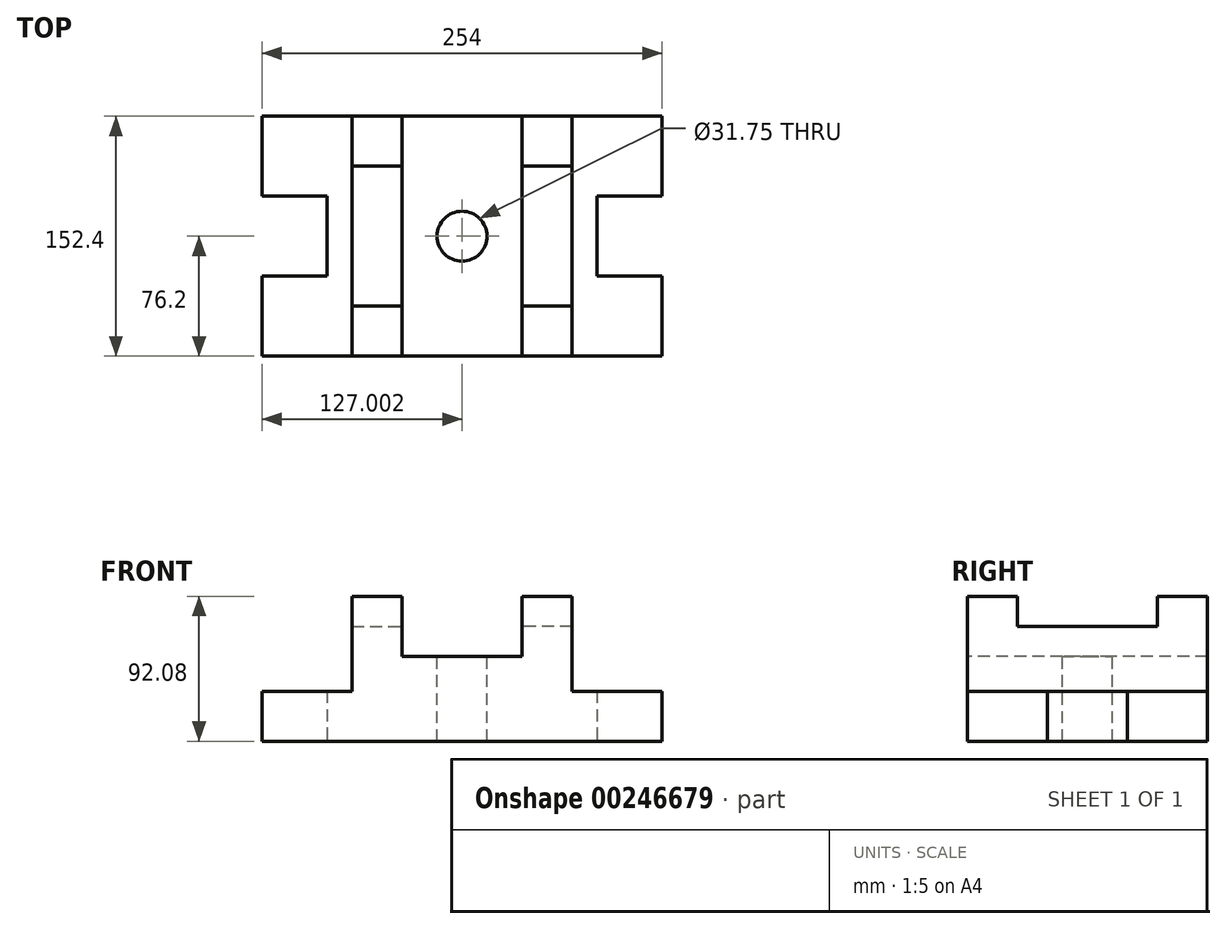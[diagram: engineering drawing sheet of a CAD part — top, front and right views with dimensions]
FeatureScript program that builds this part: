
annotation { "Feature Type Name" : "Feature", "Feature Type Description" : "" }
export const myFeature = defineFeature(function(context is Context, id is Id, definition is map)
    precondition{}
    {
        {
            var Q0;
            Q0=qCreatedBy(makeId("Top.planeOp"),FACE);
            var sketch = newSketch(context, id + "F0", { "sketchPlane" : qUnion([Q0])});
            skLineSegment(sketch, "E0.bottom", {"start": v(-124.69, 50.8) * mm, "end": v(129.31, 50.8) * mm});
            skLineSegment(sketch, "E0.top", {"start": v(-124.69, -101.6) * mm, "end": v(129.31, -101.6) * mm});
            skLineSegment(sketch, "E0.left", {"start": v(-124.69, 50.8) * mm, "end": v(-124.69, 0) * mm});
            skLineSegment(sketch, "E0.right", {"start": v(129.31, 50.8) * mm, "end": v(129.31, 0) * mm});
            skLineSegment(sketch, "E1", {"start": v(129.31, -101.6) * mm, "end": v(129.31, -50.8) * mm});
            skLineSegment(sketch, "E2", {"start": v(129.31, -50.8) * mm, "end": v(88.04, -50.8) * mm});
            skLineSegment(sketch, "E3", {"start": v(129.31, 0) * mm, "end": v(88.04, 0) * mm});
            skLineSegment(sketch, "E4", {"start": v(88.04, 0) * mm, "end": v(88.04, -50.8) * mm});
            skLineSegment(sketch, "E5.trimOffspring", {"start": v(129.31, -50.8) * mm, "end": v(129.31, -101.6) * mm});
            skLineSegment(sketch, "E6", {"start": v(-124.69, -101.6) * mm, "end": v(-124.69, -50.8) * mm});
            skLineSegment(sketch, "E7", {"start": v(-124.69, -50.8) * mm, "end": v(-83.41, -50.8) * mm});
            skLineSegment(sketch, "E8", {"start": v(-124.69, 0) * mm, "end": v(-83.41, 0) * mm});
            skLineSegment(sketch, "E9", {"start": v(-83.41, 0) * mm, "end": v(-83.41, -50.8) * mm});
            skLineSegment(sketch, "E10.trimOffspring", {"start": v(-124.69, -50.8) * mm, "end": v(-124.69, -101.6) * mm});
            skSolve(sketch);
        }
        {
            var Q0;
            Q0=makeQuery(id+"F0.imprint","IMPRINT",FACE,{"disambiguationData":[TD([[makeQuery(id+"F0.imprint","IMPRINT",EDGE,{"derivedFrom":sQuery(id+"F0.wireOp",EDGE,"E0.bottom")}),-1.0]])]});
            extrude(context, id + "F1", {"entities" : qUnion([Q0]), "depth" : 31.75 * mm});
        }
        {
            var Q0;
            Q0=makeQuery(id+"F1.opExtrude","CAP_FACE",FACE,{"disambiguationData":[OSD([sQuery(id+"F0.wireOp",EDGE,"E0.bottom"),sQuery(id+"F0.wireOp",EDGE,"E0.top"),sQuery(id+"F0.wireOp",EDGE,"E0.right"),sQuery(id+"F0.wireOp",EDGE,"E2"),sQuery(id+"F0.wireOp",EDGE,"E3"),sQuery(id+"F0.wireOp",EDGE,"E4"),sQuery(id+"F0.wireOp",EDGE,"E5.trimOffspring"),sQuery(id+"F0.wireOp",EDGE,"E0.left"),sQuery(id+"F0.wireOp",EDGE,"E7"),sQuery(id+"F0.wireOp",EDGE,"E8"),sQuery(id+"F0.wireOp",EDGE,"E9"),sQuery(id+"F0.wireOp",EDGE,"E10.trimOffspring")])],"isStart":false});
            var sketch = newSketch(context, id + "F2", { "sketchPlane" : qUnion([Q0])});
            skLineSegment(sketch, "E11", {"start": v(-124.69, -101.6) * mm, "end": v(-67.54, -101.6) * mm});
            skLineSegment(sketch, "E12.bottom", {"start": v(-67.54, -101.6) * mm, "end": v(-35.79, -101.6) * mm});
            skLineSegment(sketch, "E12.top", {"start": v(-67.54, -69.85) * mm, "end": v(-35.79, -69.85) * mm});
            skLineSegment(sketch, "E12.left", {"start": v(-67.54, -101.6) * mm, "end": v(-67.54, -69.85) * mm});
            skLineSegment(sketch, "E12.right", {"start": v(-35.79, -101.6) * mm, "end": v(-35.79, -69.85) * mm});
            skLineSegment(sketch, "E13", {"start": v(129.31, -101.6) * mm, "end": v(72.16, -101.6) * mm});
            skLineSegment(sketch, "E14.bottom", {"start": v(72.16, -101.6) * mm, "end": v(40.41, -101.6) * mm});
            skLineSegment(sketch, "E14.top", {"start": v(72.16, -69.85) * mm, "end": v(40.41, -69.85) * mm});
            skLineSegment(sketch, "E14.left", {"start": v(72.16, -101.6) * mm, "end": v(72.16, -69.85) * mm});
            skLineSegment(sketch, "E14.right", {"start": v(40.41, -101.6) * mm, "end": v(40.41, -69.85) * mm});
            skLineSegment(sketch, "E15", {"start": v(-124.69, 50.8) * mm, "end": v(-67.54, 50.8) * mm});
            skLineSegment(sketch, "E16.bottom", {"start": v(-67.54, 50.8) * mm, "end": v(-35.79, 50.8) * mm});
            skLineSegment(sketch, "E16.top", {"start": v(-67.54, 19.05) * mm, "end": v(-35.79, 19.05) * mm});
            skLineSegment(sketch, "E16.left", {"start": v(-67.54, 50.8) * mm, "end": v(-67.54, 19.05) * mm});
            skLineSegment(sketch, "E16.right", {"start": v(-35.79, 50.8) * mm, "end": v(-35.79, 19.05) * mm});
            skLineSegment(sketch, "E17", {"start": v(129.31, 50.8) * mm, "end": v(72.16, 50.8) * mm});
            skLineSegment(sketch, "E18.bottom", {"start": v(72.16, 50.8) * mm, "end": v(40.41, 50.8) * mm});
            skLineSegment(sketch, "E18.top", {"start": v(72.16, 19.05) * mm, "end": v(40.41, 19.05) * mm});
            skLineSegment(sketch, "E18.left", {"start": v(72.16, 50.8) * mm, "end": v(72.16, 19.05) * mm});
            skLineSegment(sketch, "E18.right", {"start": v(40.41, 50.8) * mm, "end": v(40.41, 19.05) * mm});
            skSolve(sketch);
        }
        {
            var Q0;
            Q0=makeQuery(id+"F2.imprint","IMPRINT",FACE,{"disambiguationData":[TD([[makeQuery(id+"F2.imprint","IMPRINT",EDGE,{"derivedFrom":sQuery(id+"F2.wireOp",EDGE,"E14.bottom")}),1.0]])]});
            var Q1;
            Q1=makeQuery(id+"F2.imprint","IMPRINT",FACE,{"disambiguationData":[TD([[makeQuery(id+"F2.imprint","IMPRINT",EDGE,{"derivedFrom":sQuery(id+"F2.wireOp",EDGE,"E18.bottom")}),-1.0]])]});
            var Q2;
            Q2=makeQuery(id+"F2.imprint","IMPRINT",FACE,{"disambiguationData":[TD([[makeQuery(id+"F2.imprint","IMPRINT",EDGE,{"derivedFrom":sQuery(id+"F2.wireOp",EDGE,"E12.bottom")}),1.0]])]});
            var Q3;
            Q3=makeQuery(id+"F2.imprint","IMPRINT",FACE,{"disambiguationData":[TD([[makeQuery(id+"F2.imprint","IMPRINT",EDGE,{"derivedFrom":sQuery(id+"F2.wireOp",EDGE,"E16.bottom")}),-1.0]])]});
            extrude(context, id + "F3", {"entities" : qUnion([Q0, Q1, Q2, Q3]), "operationType" : NewBodyOperationType.ADD, "depth" : 60.32 * mm});
        }
        {
            var Q0;
            Q0=makeQuery(id+"F1.opExtrude","CAP_FACE",FACE,{"disambiguationData":[OSD([sQuery(id+"F0.wireOp",EDGE,"E0.bottom"),sQuery(id+"F0.wireOp",EDGE,"E0.top"),sQuery(id+"F0.wireOp",EDGE,"E0.right"),sQuery(id+"F0.wireOp",EDGE,"E2"),sQuery(id+"F0.wireOp",EDGE,"E3"),sQuery(id+"F0.wireOp",EDGE,"E4"),sQuery(id+"F0.wireOp",EDGE,"E5.trimOffspring"),sQuery(id+"F0.wireOp",EDGE,"E0.left"),sQuery(id+"F0.wireOp",EDGE,"E7"),sQuery(id+"F0.wireOp",EDGE,"E8"),sQuery(id+"F0.wireOp",EDGE,"E9"),sQuery(id+"F0.wireOp",EDGE,"E10.trimOffspring")])],"isStart":false});
            var sketch = newSketch(context, id + "F4", { "sketchPlane" : qUnion([Q0])});
            skLineSegment(sketch, "E19.bottom", {"start": v(-35.79, 19.05) * mm, "end": v(40.41, 19.05) * mm});
            skLineSegment(sketch, "E19.top", {"start": v(-35.79, 50.8) * mm, "end": v(40.41, 50.8) * mm});
            skLineSegment(sketch, "E19.left", {"start": v(-35.79, 19.05) * mm, "end": v(-35.79, 50.8) * mm});
            skLineSegment(sketch, "E19.right", {"start": v(40.41, 19.05) * mm, "end": v(40.41, 50.8) * mm});
            skLineSegment(sketch, "E20.bottom", {"start": v(40.41, 19.05) * mm, "end": v(72.16, 19.05) * mm});
            skLineSegment(sketch, "E20.top", {"start": v(40.41, -69.85) * mm, "end": v(72.16, -69.85) * mm});
            skLineSegment(sketch, "E20.left", {"start": v(40.41, 19.05) * mm, "end": v(40.41, -69.85) * mm});
            skLineSegment(sketch, "E20.right", {"start": v(72.16, 19.05) * mm, "end": v(72.16, -69.85) * mm});
            skLineSegment(sketch, "E21.bottom", {"start": v(-35.79, -69.85) * mm, "end": v(40.41, -69.85) * mm});
            skLineSegment(sketch, "E21.top", {"start": v(-35.79, -101.6) * mm, "end": v(40.41, -101.6) * mm});
            skLineSegment(sketch, "E21.left", {"start": v(-35.79, -69.85) * mm, "end": v(-35.79, -101.6) * mm});
            skLineSegment(sketch, "E21.right", {"start": v(40.41, -69.85) * mm, "end": v(40.41, -101.6) * mm});
            skLineSegment(sketch, "E22.bottom", {"start": v(-67.54, -69.85) * mm, "end": v(-35.79, -69.85) * mm});
            skLineSegment(sketch, "E22.top", {"start": v(-67.54, 19.05) * mm, "end": v(-35.79, 19.05) * mm});
            skLineSegment(sketch, "E22.left", {"start": v(-67.54, -69.85) * mm, "end": v(-67.54, 19.05) * mm});
            skLineSegment(sketch, "E22.right", {"start": v(-35.79, -69.85) * mm, "end": v(-35.79, 19.05) * mm});
            skSolve(sketch);
        }
        {
            var Q0;
            Q0=makeQuery(id+"F4.imprint","IMPRINT",FACE,{"disambiguationData":[TD([[makeQuery(id+"F4.imprint","IMPRINT",EDGE,{"derivedFrom":sQuery(id+"F4.wireOp",EDGE,"E19.bottom")}),1.0]])]});
            var Q1;
            Q1=makeQuery(id+"F4.imprint","IMPRINT",FACE,{"disambiguationData":[TD([[makeQuery(id+"F4.imprint","IMPRINT",EDGE,{"derivedFrom":sQuery(id+"F4.wireOp",EDGE,"E21.bottom")}),-1.0]])]});
            var Q2;
            Q2=makeQuery(id+"F4.imprint","IMPRINT",FACE,{"disambiguationData":[TD([[makeQuery(id+"F4.imprint","IMPRINT",EDGE,{"derivedFrom":sQuery(id+"F4.wireOp",EDGE,"E20.bottom")}),1.0]])]});
            var Q3;
            Q3=makeQuery(id+"F4.imprint","IMPRINT",FACE,{"disambiguationData":[TD([[makeQuery(id+"F4.imprint","IMPRINT",EDGE,{"derivedFrom":sQuery(id+"F4.wireOp",EDGE,"E19.bottom")}),-1.0]])]});
            var Q4;
            Q4=makeQuery(id+"F4.imprint","IMPRINT",FACE,{"disambiguationData":[TD([[makeQuery(id+"F4.imprint","IMPRINT",EDGE,{"derivedFrom":sQuery(id+"F4.wireOp",EDGE,"E22.bottom")}),1.0]])]});
            extrude(context, id + "F5", {"entities" : qUnion([Q0, Q1, Q2, Q3, Q4]), "operationType" : NewBodyOperationType.ADD, "depth" : 22.22 * mm});
        }
        {
            var Q0;
            Q0=makeQuery(id+"F5.opExtrude","CAP_FACE",FACE,{"disambiguationData":[OSD([sQuery(id+"F4.wireOp",EDGE,"E19.top"),sQuery(id+"F4.wireOp",EDGE,"E19.left"),sQuery(id+"F4.wireOp",EDGE,"E19.right"),sQuery(id+"F4.wireOp",EDGE,"E20.bottom"),sQuery(id+"F4.wireOp",EDGE,"E20.top"),sQuery(id+"F4.wireOp",EDGE,"E20.right"),sQuery(id+"F4.wireOp",EDGE,"E21.top"),sQuery(id+"F4.wireOp",EDGE,"E21.left"),sQuery(id+"F4.wireOp",EDGE,"E21.right"),sQuery(id+"F4.wireOp",EDGE,"E22.bottom"),sQuery(id+"F4.wireOp",EDGE,"E22.top"),sQuery(id+"F4.wireOp",EDGE,"E22.left")])],"isStart":false});
            var sketch = newSketch(context, id + "F6", { "sketchPlane" : qUnion([Q0])});
            skLineSegment(sketch, "E23.bottom", {"start": v(-67.54, 19.05) * mm, "end": v(-35.79, 19.05) * mm});
            skLineSegment(sketch, "E23.top", {"start": v(-67.54, -69.85) * mm, "end": v(-35.79, -69.85) * mm});
            skLineSegment(sketch, "E23.left", {"start": v(-67.54, 19.05) * mm, "end": v(-67.54, -69.85) * mm});
            skLineSegment(sketch, "E23.right", {"start": v(-35.79, 19.05) * mm, "end": v(-35.79, -69.85) * mm});
            skLineSegment(sketch, "E24.bottom", {"start": v(40.41, 19.05) * mm, "end": v(72.16, 19.05) * mm});
            skLineSegment(sketch, "E24.top", {"start": v(40.41, -69.85) * mm, "end": v(72.16, -69.85) * mm});
            skLineSegment(sketch, "E24.left", {"start": v(40.41, 19.05) * mm, "end": v(40.41, -69.85) * mm});
            skLineSegment(sketch, "E24.right", {"start": v(72.16, 19.05) * mm, "end": v(72.16, -69.85) * mm});
            skSolve(sketch);
        }
        {
            var Q0;
            Q0=makeQuery(id+"F6.imprint","IMPRINT",FACE,{"disambiguationData":[TD([[makeQuery(id+"F6.imprint","IMPRINT",EDGE,{"derivedFrom":sQuery(id+"F6.wireOp",EDGE,"E24.bottom")}),1.0]])]});
            var Q1;
            Q1=makeQuery(id+"F6.imprint","IMPRINT",FACE,{"disambiguationData":[TD([[makeQuery(id+"F6.imprint","IMPRINT",EDGE,{"derivedFrom":sQuery(id+"F6.wireOp",EDGE,"E23.bottom")}),-1.0]])]});
            extrude(context, id + "F7", {"entities" : qUnion([Q0, Q1]), "operationType" : NewBodyOperationType.ADD, "depth" : 19.05 * mm});
        }
        {
            var Q0;
            Q0=makeQuery(id+"F5.opExtrude","CAP_FACE",FACE,{"disambiguationData":[OSD([sQuery(id+"F4.wireOp",EDGE,"E19.top"),sQuery(id+"F4.wireOp",EDGE,"E19.left"),sQuery(id+"F4.wireOp",EDGE,"E19.right"),sQuery(id+"F4.wireOp",EDGE,"E20.bottom"),sQuery(id+"F4.wireOp",EDGE,"E20.top"),sQuery(id+"F4.wireOp",EDGE,"E20.right"),sQuery(id+"F4.wireOp",EDGE,"E21.top"),sQuery(id+"F4.wireOp",EDGE,"E21.left"),sQuery(id+"F4.wireOp",EDGE,"E21.right"),sQuery(id+"F4.wireOp",EDGE,"E22.bottom"),sQuery(id+"F4.wireOp",EDGE,"E22.top"),sQuery(id+"F4.wireOp",EDGE,"E22.left")])],"isStart":false});
            var sketch = newSketch(context, id + "F8", { "sketchPlane" : qUnion([Q0])});
            skLineSegment(sketch, "E25", {"start": v(2.31, -101.6) * mm, "end": v(2.31, -25.4) * mm});
            skCircle(sketch, "E26", {"center": v(2.31, -25.4) * mm, "radius": 15.88 * mm});
            skSolve(sketch);
        }
        {
            var Q0;
            Q0 = qSketchRegion(id + "F8", true);
            extrude(context, id + "F9", {"entities" : qUnion([Q0]), "operationType" : NewBodyOperationType.REMOVE, "oppositeDirection" : true, "depth" : 53.97 * mm});
        }
    });
